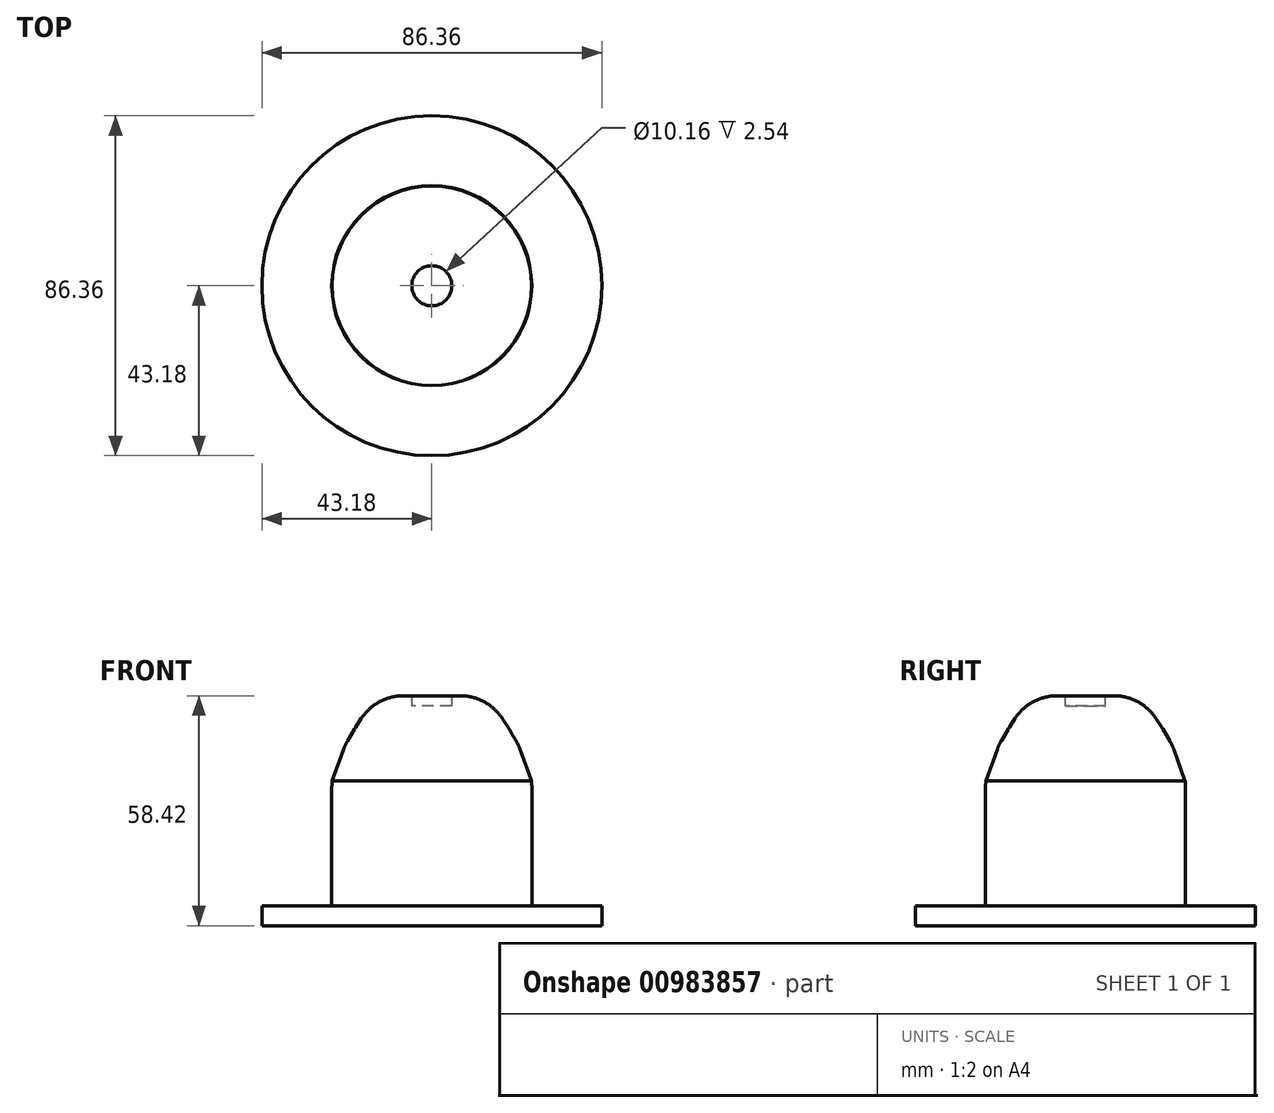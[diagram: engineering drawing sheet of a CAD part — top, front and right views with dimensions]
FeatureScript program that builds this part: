
annotation { "Feature Type Name" : "Feature", "Feature Type Description" : "" }
export const myFeature = defineFeature(function(context is Context, id is Id, definition is map)
    precondition{}
    {
        {
            var Q0;
            Q0=qCreatedBy(makeId("Top.planeOp"),FACE);
            var sketch = newSketch(context, id + "F0", { "sketchPlane" : qUnion([Q0])});
            skCircle(sketch, "E0", {"center": v(0, 0) * mm, "radius": 43.18 * mm});
            skCircle(sketch, "E1", {"center": v(0, 0) * mm, "radius": 25.4 * mm});
            skSolve(sketch);
        }
        {
            var Q0;
            Q0 = qSketchRegion(id + "F0", true);
            extrude(context, id + "F1", {"entities" : qUnion([Q0]), "depth" : 5.08 * mm, "offsetDistance" : 25.4 * mm});
        }
        {
            var Q0;
            Q0=makeQuery(id+"F0.imprint","IMPRINT",FACE,{"disambiguationData":[TD([[makeQuery(id+"F0.imprint","IMPRINT",EDGE,{"derivedFrom":sQuery(id+"F0.wireOp",EDGE,"E1")}),1.0]])]});
            extrude(context, id + "F2", {"entities" : qUnion([Q0]), "operationType" : NewBodyOperationType.ADD, "depth" : 36.83 * mm, "offsetDistance" : 25.4 * mm});
        }
        {
            var Q0;
            Q0=qCreatedBy(makeId("Front.planeOp"),FACE);
            var sketch = newSketch(context, id + "F3", { "sketchPlane" : qUnion([Q0])});
            skLineSegment(sketch, "E2", {"start": v(0, 58.42) * mm, "end": v(0, 0) * mm, "construction": true});
            skLineSegment(sketch, "E3", {"start": v(0, 36.83) * mm, "end": v(0, 58.42) * mm});
            skLineSegment(sketch, "E4", {"start": v(0, 58.42) * mm, "end": v(11.05, 58.42) * mm});
            skLineSegment(sketch, "E5", {"start": v(11.05, 58.42) * mm, "end": v(16.47, 54.87) * mm});
            skLineSegment(sketch, "E6", {"start": v(16.47, 54.87) * mm, "end": v(19.52, 50.17) * mm});
            skLineSegment(sketch, "E7", {"start": v(19.52, 50.17) * mm, "end": v(22.03, 45.93) * mm});
            skLineSegment(sketch, "E8", {"start": v(22.03, 45.93) * mm, "end": v(25.34, 36.74) * mm});
            skLineSegment(sketch, "E9", {"start": v(25.34, 36.74) * mm, "end": v(0, 36.83) * mm});
            skSolve(sketch);
        }
        {
            var Q0;
            Q0=makeQuery(id+"F3.imprint","IMPRINT",FACE,{"disambiguationData":[TD([[makeQuery(id+"F3.imprint","IMPRINT",EDGE,{"derivedFrom":sQuery(id+"F3.wireOp",EDGE,"E3")}),-1.0]])]});
            var Q1;
            Q1=sQuery(id+"F3.wireOp",EDGE,"E3");
            revolve(context, id + "F4", {"operationType" : NewBodyOperationType.ADD, "surfaceOperationType" : NewSurfaceOperationType.NEW, "entities" : qUnion([Q0]), "axis" : qUnion([Q1]), "revolveType" : RevolveType.FULL});
        }
        {
            var Q0;
            Q0=makeQuery(id+"F2.opExtrude","CAP_EDGE",EDGE,{"disambiguationData":[OSD([sQuery(id+"F0.wireOp",EDGE,"E1")])],"isStart":false});
            var Q1;
            Q1=makeQuery(id+"F4.opRevolve","SWEPT_EDGE",EDGE,{"disambiguationData":[OSD([sQuery(id+"F3.wireOp",EDGE,"E6"),sQuery(id+"F3.wireOp",EDGE,"E7")])]});
            var Q2;
            Q2=makeQuery(id+"F4.opRevolve","SWEPT_EDGE",EDGE,{"disambiguationData":[OSD([sQuery(id+"F3.wireOp",EDGE,"E7"),sQuery(id+"F3.wireOp",EDGE,"E8")])]});
            var Q3;
            Q3=makeQuery(id+"F4.opRevolve","SWEPT_EDGE",EDGE,{"disambiguationData":[OSD([sQuery(id+"F3.wireOp",EDGE,"E5"),sQuery(id+"F3.wireOp",EDGE,"E6")])]});
            var Q4;
            Q4=makeQuery(id+"F4.opRevolve","SWEPT_EDGE",EDGE,{"disambiguationData":[OSD([sQuery(id+"F3.wireOp",EDGE,"E4"),sQuery(id+"F3.wireOp",EDGE,"E5")])]});
            fillet(context, id + "F5", {"entities" : qUnion([Q0, Q1, Q2, Q3, Q4]), "radius" : 12.7 * mm, "tangentPropagation" : true, "allowEdgeOverflow" : false});
        }
        {
            var Q0;
            Q0=makeQuery(id+"F4.opRevolve","SWEPT_FACE",FACE,{"disambiguationData":[OSD([sQuery(id+"F3.wireOp",EDGE,"E4")])]});
            var sketch = newSketch(context, id + "F6", { "sketchPlane" : qUnion([Q0])});
            skCircle(sketch, "E10", {"center": v(0, 0) * mm, "radius": 5.08 * mm});
            skSolve(sketch);
        }
        {
            var Q0;
            Q0=makeQuery(id+"F6.imprint","IMPRINT",FACE,{"disambiguationData":[TD([[makeQuery(id+"F6.imprint","IMPRINT",EDGE,{"derivedFrom":sQuery(id+"F6.wireOp",EDGE,"E10")}),1.0]])]});
            extrude(context, id + "F7", {"entities" : qUnion([Q0]), "operationType" : NewBodyOperationType.REMOVE, "oppositeDirection" : true, "depth" : 2.54 * mm, "offsetDistance" : 25.4 * mm});
        }
    });
